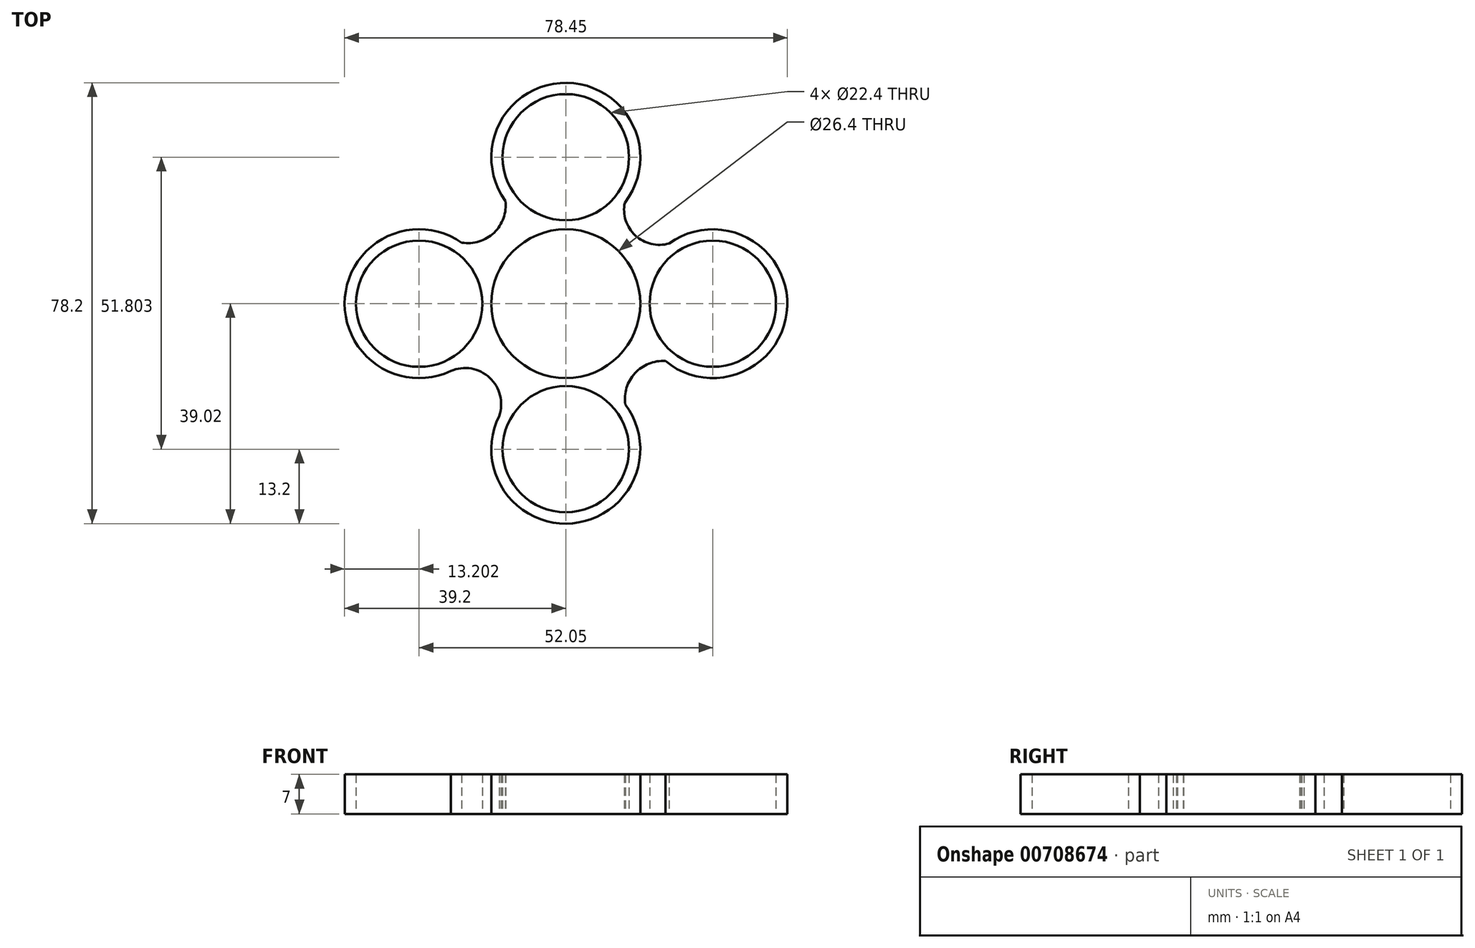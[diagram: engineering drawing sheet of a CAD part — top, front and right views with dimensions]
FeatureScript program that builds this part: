
annotation { "Feature Type Name" : "Feature", "Feature Type Description" : "" }
export const myFeature = defineFeature(function(context is Context, id is Id, definition is map)
    precondition{}
    {
        {
            var Q0;
            Q0=qCreatedBy(makeId("Top.planeOp"),FACE);
            var sketch = newSketch(context, id + "F0", { "sketchPlane" : qUnion([Q0])});
            skCircle(sketch, "E0", {"center": v(0, 0) * mm, "radius": 11.2 * mm});
            skCircle(sketch, "E1", {"center": v(0, 0) * mm, "radius": 13.2 * mm});
            skCircle(sketch, "E2", {"center": v(-26, 0) * mm, "radius": 11.2 * mm});
            skCircle(sketch, "E3", {"center": v(-26, 0) * mm, "radius": 13.2 * mm});
            skCircle(sketch, "E4", {"center": v(26.05, 0) * mm, "radius": 11.2 * mm});
            skCircle(sketch, "E5", {"center": v(26.05, 0) * mm, "radius": 13.2 * mm});
            skCircle(sketch, "E6", {"center": v(0, 25.98) * mm, "radius": 11.2 * mm});
            skCircle(sketch, "E7", {"center": v(0, 25.98) * mm, "radius": 13.2 * mm});
            skCircle(sketch, "E8", {"center": v(0, -25.82) * mm, "radius": 11.2 * mm});
            skCircle(sketch, "E9", {"center": v(0, -25.82) * mm, "radius": 13.2 * mm});
            skArc(sketch, "E10", {"start": v(-21.95, 12.56) * mm, "mid": v(-12.53, 12.78) * mm, "end": v(-12.65, 22.2) * mm});
            skArc(sketch, "E11", {"start": v(-11.8, -19.92) * mm, "mid": v(-13.58, -13.05) * mm, "end": v(-20.6, -12.05) * mm});
            skArc(sketch, "E12", {"start": v(22.5, -12.71) * mm, "mid": v(12.68, -11.92) * mm, "end": v(12.56, -21.77) * mm});
            skArc(sketch, "E13", {"start": v(12.3, 21.2) * mm, "mid": v(12, 12.4) * mm, "end": v(20.8, 12.11) * mm});
            skSolve(sketch);
        }
        {
            var Q0;
            Q0=qSketchRegion(id+"F0",true);
            extrude(context, id + "F1", {"entities" : qUnion([Q0]), "depth" : 7 * mm, "offsetDistance" : 25 * mm});
        }
    });
